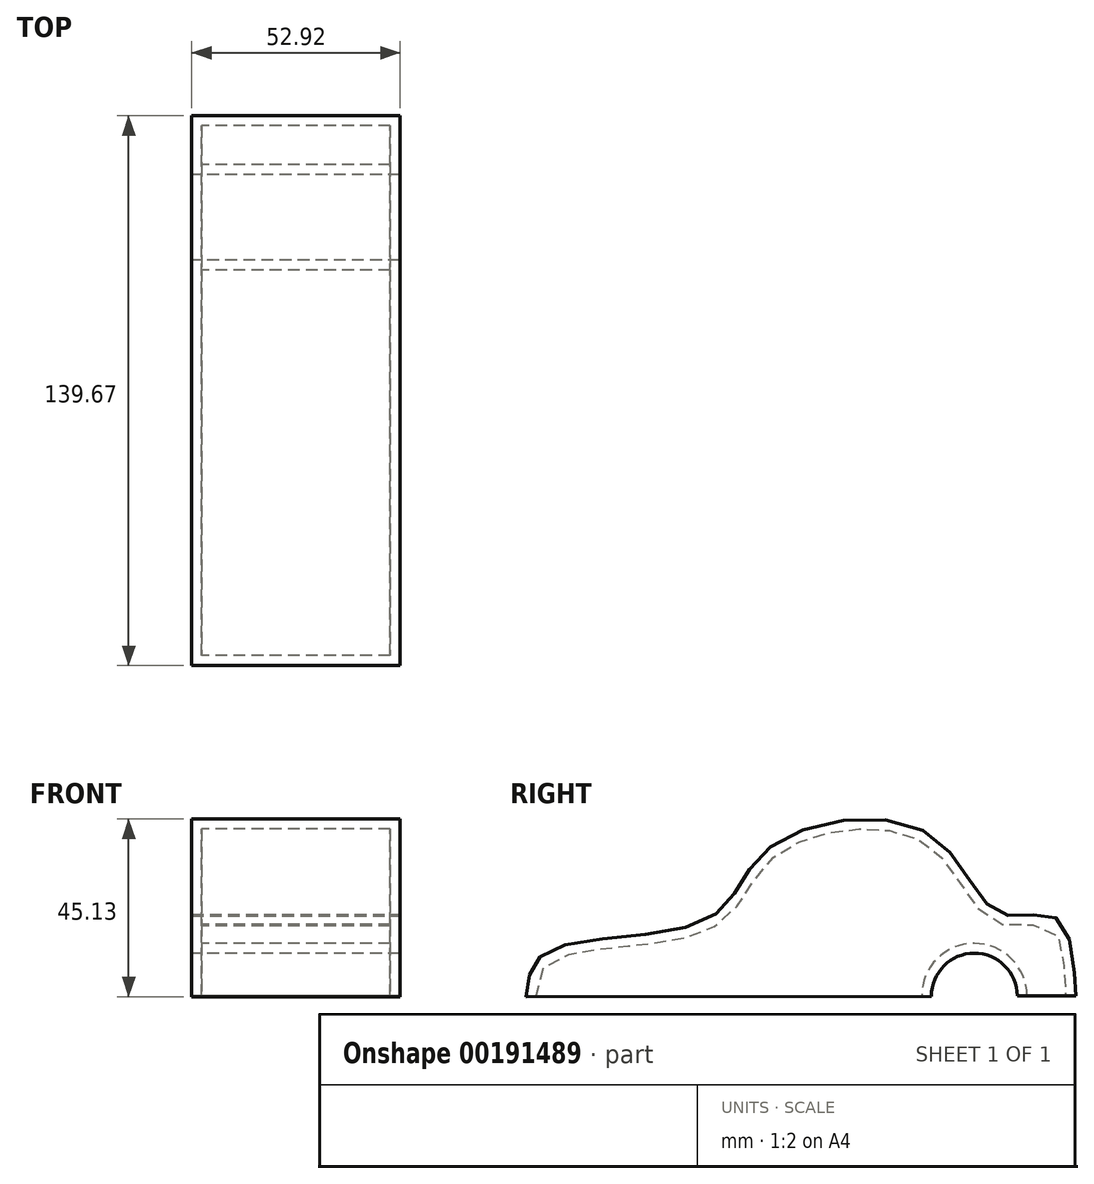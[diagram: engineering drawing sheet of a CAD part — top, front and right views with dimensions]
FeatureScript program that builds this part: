
annotation { "Feature Type Name" : "Feature", "Feature Type Description" : "" }
export const myFeature = defineFeature(function(context is Context, id is Id, definition is map)
    precondition{}
    {
        {
            var Q0;
            Q0=qCreatedBy(makeId("Right.planeOp"),FACE);
            var sketch = newSketch(context, id + "F0", { "sketchPlane" : qUnion([Q0])});
            skFitSpline(sketch, "E0", {"points": [v(-66.36, -2.27) * mm, v(-60.8, 9.24) * mm, v(-20.14, 17.48) * mm, v(-4.6, 35.51) * mm, v(36.25, 38.96) * mm, v(54.27, 18.83) * mm, v(69.8, 16.52) * mm, v(73.45, -2.46) * mm, v(73.64, -2.08) * mm, v(73.45, -2.08) * mm], "startDerivative": vector(13.4, 135.32) * mm, "endDerivative": vector(-21.35, -7.69) * mm});
            skLineSegment(sketch, "E1", {"start": v(73.64, -2.08) * mm, "end": v(-66.36, -2.27) * mm});
            skCircle(sketch, "E2", {"center": v(-34.56, -2.23) * mm, "radius": 12 * mm});
            skCircle(sketch, "E3", {"center": v(47.54, -2.11) * mm, "radius": 10.88 * mm});
            skSolve(sketch);
        }
        {
            var Q0;
            {var subQ0=sQuery(id+"F0.wireOp",EDGE,"E1");var subQ1=sQuery(id+"F0.wireOp",EDGE,"E0");var subQ5=makeQuery(id+"F0.imprint","INTERSECT",VERTEX,{"disambiguationData":[OD(0.0)],"derivedFrom":[subQ1,subQ0]});Q0=makeQuery(id+"F0.imprint","IMPRINT",FACE,{"disambiguationData":[TD([[makeQuery(id+"F0.imprint","IMPRINT",EDGE,{"disambiguationData":[TD([[subQ5,-1.0]])],"derivedFrom":subQ1}),-1.0]])]});}
            var Q1;
            {var subQ0=sQuery(id+"F0.wireOp",EDGE,"E3");var subQ1=sQuery(id+"F0.wireOp",EDGE,"E1");var subQ2=makeQuery(id+"F0.imprint","INTERSECT",VERTEX,{"disambiguationData":[OD(0.0)],"derivedFrom":[subQ1,subQ0]});Q1=makeQuery(id+"F0.imprint","IMPRINT",FACE,{"disambiguationData":[TD([[makeQuery(id+"F0.imprint","IMPRINT",EDGE,{"disambiguationData":[TD([[subQ2,-1.0]])],"derivedFrom":subQ1}),-1.0]])]});}
            var Q2;
            {var subQ0=sQuery(id+"F0.wireOp",EDGE,"E2");var subQ1=sQuery(id+"F0.wireOp",EDGE,"E1");var subQ2=makeQuery(id+"F0.imprint","INTERSECT",VERTEX,{"disambiguationData":[OD(0.0)],"derivedFrom":[subQ1,subQ0]});Q2=makeQuery(id+"F0.imprint","IMPRINT",FACE,{"disambiguationData":[TD([[makeQuery(id+"F0.imprint","IMPRINT",EDGE,{"disambiguationData":[TD([[subQ2,-1.0]])],"derivedFrom":subQ1}),-1.0]])]});}
            extrude(context, id + "F1", {"entities" : qUnion([Q0, Q1, Q2]), "endBound" : BoundingType.SYMMETRIC, "depth" : 52.9 * mm});
        }
        {
            var Q0;
            Q0=makeQuery(id+"F1.opExtrude","SWEPT_FACE",FACE,{"disambiguationData":[OSD([sQuery(id+"F0.wireOp",EDGE,"E1")])]});
            shell(context, id + "F2", {"entities" : qUnion([Q0]), "thickness" : 2.5 * mm});
        }
    });
